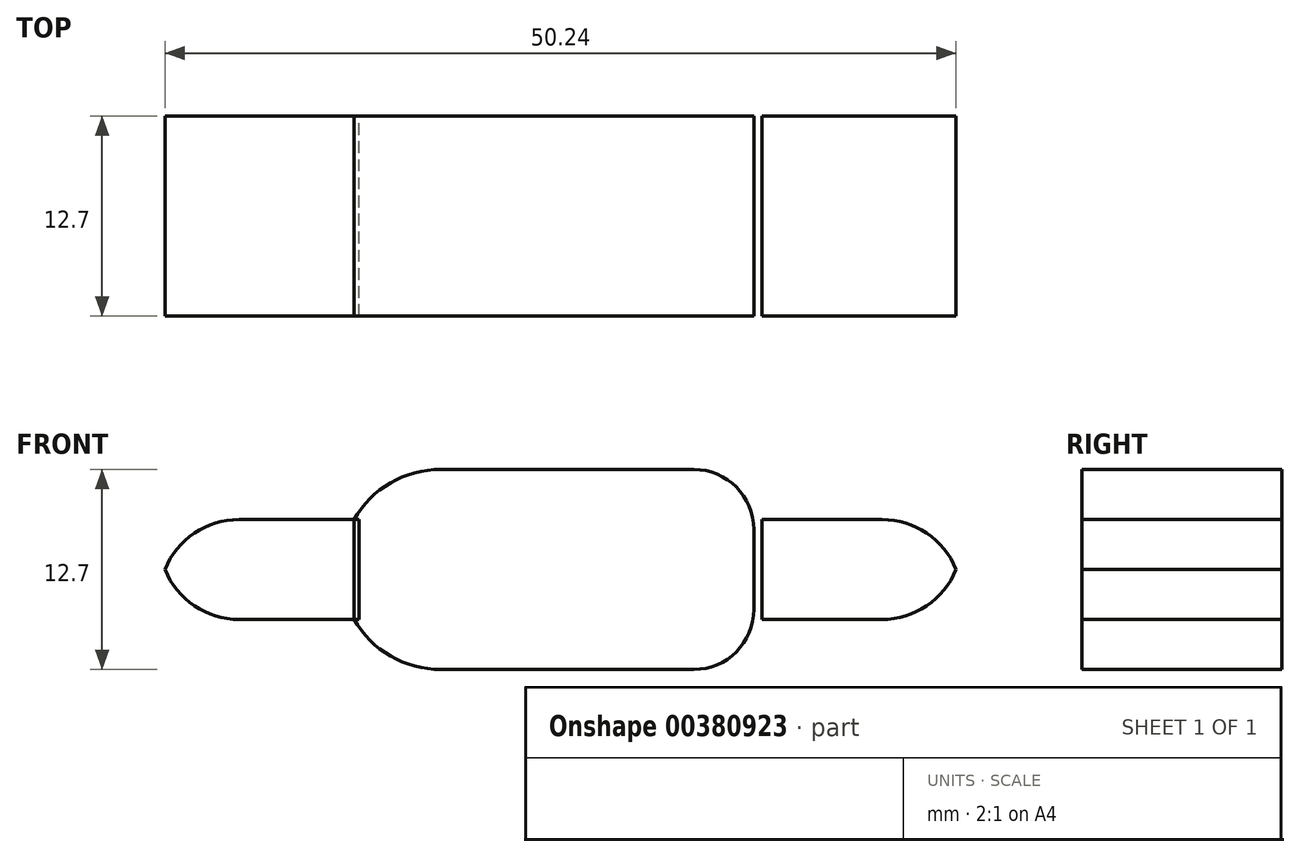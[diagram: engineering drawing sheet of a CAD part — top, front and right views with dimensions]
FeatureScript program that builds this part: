
annotation { "Feature Type Name" : "Feature", "Feature Type Description" : "" }
export const myFeature = defineFeature(function(context is Context, id is Id, definition is map)
    precondition{}
    {
        {
            var Q0;
            Q0=qCreatedBy(makeId("Front.planeOp"),FACE);
            var sketch = newSketch(context, id + "F0", { "sketchPlane" : qUnion([Q0])});
            skLineSegment(sketch, "E0.bottom", {"start": v(12.7, -6.35) * mm, "end": v(-12.7, -6.35) * mm});
            skLineSegment(sketch, "E0.top", {"start": v(12.7, 6.35) * mm, "end": v(-12.7, 6.35) * mm});
            skLineSegment(sketch, "E0.left", {"start": v(12.7, -6.35) * mm, "end": v(12.7, 6.35) * mm});
            skLineSegment(sketch, "E0.right", {"start": v(-12.7, -6.35) * mm, "end": v(-12.7, 6.35) * mm});
            skPoint(sketch, "E0.middle", {"position": v(0, 0) * mm});
            skLineSegment(sketch, "E1.bottom", {"start": v(-25.07, 3.17) * mm, "end": v(-12.37, 3.17) * mm});
            skLineSegment(sketch, "E1.top", {"start": v(-25.07, -3.18) * mm, "end": v(-12.37, -3.18) * mm});
            skLineSegment(sketch, "E1.left", {"start": v(-25.07, 3.17) * mm, "end": v(-25.07, -3.18) * mm});
            skLineSegment(sketch, "E1.right", {"start": v(-12.37, 3.17) * mm, "end": v(-12.37, -3.18) * mm});
            skPoint(sketch, "E1.middle", {"position": v(-18.72, 0) * mm});
            skPoint(sketch, "E2", {"position": v(-12.7, 0) * mm});
            skLineSegment(sketch, "E3.bottom", {"start": v(25.91, -3.18) * mm, "end": v(13.21, -3.18) * mm});
            skLineSegment(sketch, "E3.top", {"start": v(25.91, 3.18) * mm, "end": v(13.21, 3.17) * mm});
            skLineSegment(sketch, "E3.left", {"start": v(25.91, -3.17) * mm, "end": v(25.91, 3.18) * mm});
            skLineSegment(sketch, "E3.right", {"start": v(13.21, -3.18) * mm, "end": v(13.21, 3.18) * mm});
            skPoint(sketch, "E3.middle", {"position": v(19.56, 0) * mm});
            skSolve(sketch);
        }
        {
            var Q0;
            Q0=makeQuery(id+"F0.imprint","IMPRINT",FACE,{"disambiguationData":[TD([[makeQuery(id+"F0.imprint","IMPRINT",EDGE,{"derivedFrom":sQuery(id+"F0.wireOp",EDGE,"E3.bottom")}),-1.0]])]});
            var Q1;
            {var subQ5=sQuery(id+"F0.wireOp",EDGE,"E1.left");Q1=makeQuery(id+"F0.imprint","IMPRINT",FACE,{"disambiguationData":[TD([[makeQuery(id+"F0.imprint","IMPRINT",EDGE,{"derivedFrom":subQ5}),1.0]])]});}
            var Q2;
            {var subQ1=sQuery(id+"F0.wireOp",EDGE,"E0.bottom");Q2=makeQuery(id+"F0.imprint","IMPRINT",FACE,{"disambiguationData":[TD([[makeQuery(id+"F0.imprint","IMPRINT",EDGE,{"derivedFrom":subQ1}),-1.0]])]});}
            extrude(context, id + "F1", {"entities" : qUnion([Q0, Q1, Q2]), "depth" : 12.7 * mm});
        }
        {
            var Q0;
            Q0=makeQuery(id+"F1.opExtrude","SWEPT_EDGE",EDGE,{"disambiguationData":[OSD([sQuery(id+"F0.wireOp",EDGE,"E0.top"),sQuery(id+"F0.wireOp",EDGE,"E0.right")])]});
            var Q1;
            Q1=makeQuery(id+"F1.opExtrude","SWEPT_EDGE",EDGE,{"disambiguationData":[OSD([sQuery(id+"F0.wireOp",EDGE,"E0.bottom"),sQuery(id+"F0.wireOp",EDGE,"E0.right")])]});
            fillet(context, id + "F2", {"entities" : qUnion([Q0, Q1]), "radius" : 6.35 * mm, "tangentPropagation" : true, "allowEdgeOverflow" : false});
        }
        {
            var Q0;
            Q0=makeQuery(id+"F1.opExtrude","SWEPT_EDGE",EDGE,{"disambiguationData":[OSD([sQuery(id+"F0.wireOp",EDGE,"E1.top"),sQuery(id+"F0.wireOp",EDGE,"E1.left")])]});
            var Q1;
            Q1=makeQuery(id+"F1.opExtrude","SWEPT_EDGE",EDGE,{"disambiguationData":[OSD([sQuery(id+"F0.wireOp",EDGE,"E1.bottom"),sQuery(id+"F0.wireOp",EDGE,"E1.left")])]});
            var Q2;
            Q2=makeQuery(id+"F1.opExtrude","SWEPT_EDGE",EDGE,{"disambiguationData":[OSD([sQuery(id+"F0.wireOp",EDGE,"E3.bottom"),sQuery(id+"F0.wireOp",EDGE,"E3.left")])]});
            var Q3;
            Q3=makeQuery(id+"F1.opExtrude","SWEPT_EDGE",EDGE,{"disambiguationData":[OSD([sQuery(id+"F0.wireOp",EDGE,"E3.top"),sQuery(id+"F0.wireOp",EDGE,"E3.left")])]});
            fillet(context, id + "F3", {"entities" : qUnion([Q0, Q1, Q2, Q3]), "radius" : 5.08 * mm, "tangentPropagation" : true, "allowEdgeOverflow" : false});
        }
        {
            var Q0;
            Q0=makeQuery(id+"F1.opExtrude","SWEPT_EDGE",EDGE,{"disambiguationData":[OSD([sQuery(id+"F0.wireOp",EDGE,"E0.top"),sQuery(id+"F0.wireOp",EDGE,"E0.left")])]});
            var Q1;
            Q1=makeQuery(id+"F1.opExtrude","SWEPT_EDGE",EDGE,{"disambiguationData":[OSD([sQuery(id+"F0.wireOp",EDGE,"E0.bottom"),sQuery(id+"F0.wireOp",EDGE,"E0.left")])]});
            fillet(context, id + "F4", {"entities" : qUnion([Q0, Q1]), "radius" : 3.8 * mm, "tangentPropagation" : true, "allowEdgeOverflow" : false});
        }
    });
